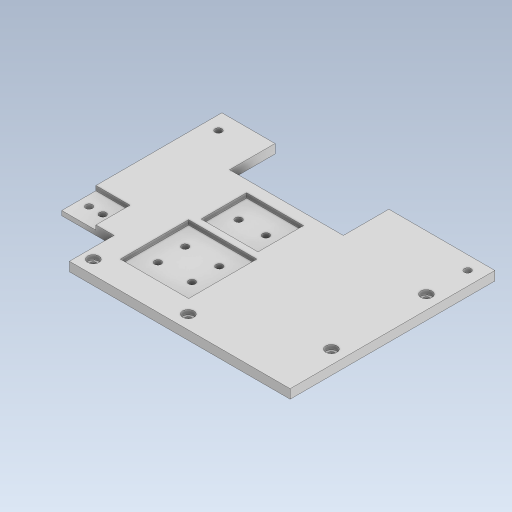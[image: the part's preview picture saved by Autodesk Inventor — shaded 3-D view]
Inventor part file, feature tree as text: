
AUTODESK INVENTOR PART (.ipt)
format: ipt  version: 2023.5 (Build 275446000, 446)  size: 356,864 bytes
history: native  units: in
note: dims shown in document units (in); Inventor stores cm internally (conversion verified against a paired STEP export)
features: extrude x2, sketch x1
ambient origin geometry x8: Origin, YZ Plane, XZ Plane, XY Plane, X Axis, Y Axis, Z Axis, Center Point
bodies: Solid1 (feature_tree)
feature tree (3):
  sketch  "Sketch1"  dims[d28=0.1575in d29=0.0in d30=0.0787in d31=0.0in d32=0.4724in d33=0.2953in d34=0.2953in d35=0.4724in d36=0.0in d37=0.0in d39=0.315in]
  extrude  "Extrusion1"  Depth=0.0787in TaperAngle=0.0deg
  extrude  "Extrusion2"  Depth=0.4724in
